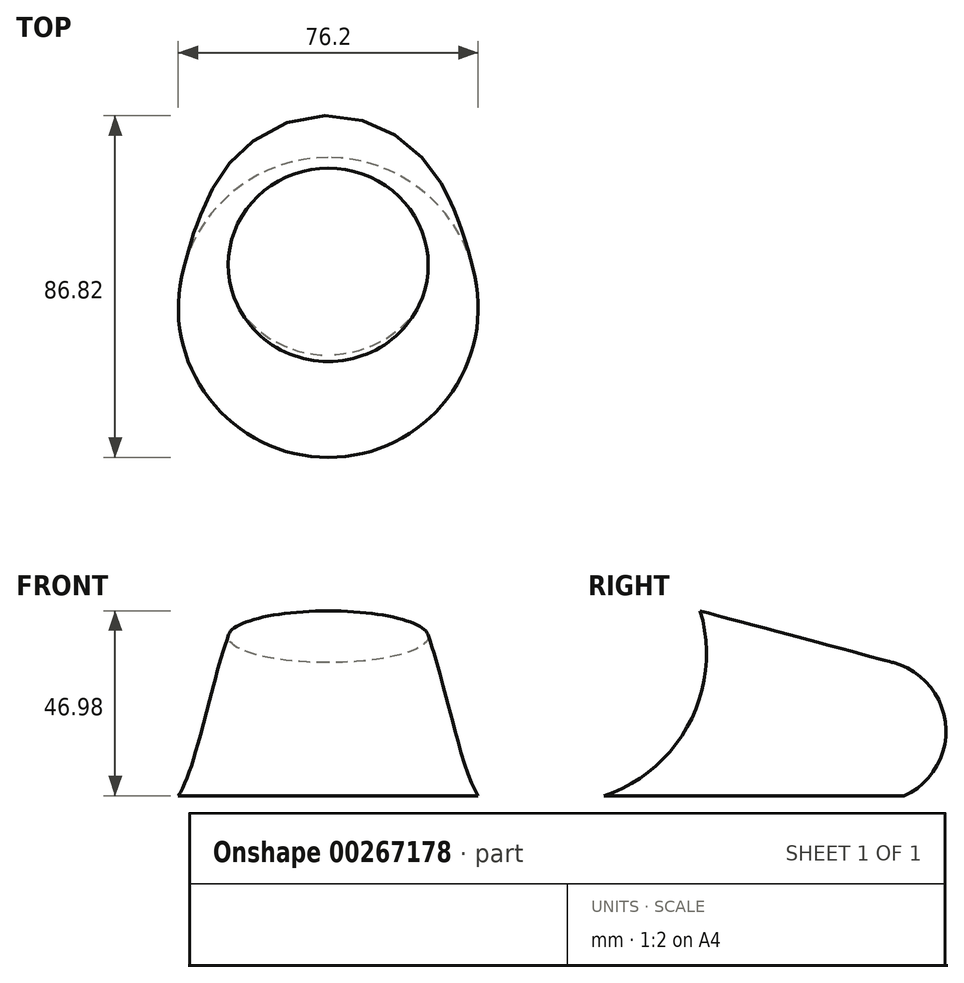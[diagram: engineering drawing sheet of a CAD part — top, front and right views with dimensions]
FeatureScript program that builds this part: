
annotation { "Feature Type Name" : "Feature", "Feature Type Description" : "" }
export const myFeature = defineFeature(function(context is Context, id is Id, definition is map)
    precondition{}
    {
        {
            var Q0;
            Q0=qCreatedBy(makeId("Top.planeOp"),FACE);
            var sketch = newSketch(context, id + "F0", { "sketchPlane" : qUnion([Q0])});
            skCircle(sketch, "E0", {"center": v(0, 0) * mm, "radius": 38.1 * mm});
            skLineSegment(sketch, "E1", {"start": v(-63.5, 63.5) * mm, "end": v(63.5, 63.5) * mm, "construction": true});
            skSolve(sketch);
        }
        {
            var Q0;
            Q0=sQuery(id+"F0.wireOp",EDGE,"E1");
            cPlane(context, id + "F1", {"entities" : qUnion([Q0]), "cplaneType" : CPlaneType.LINE_ANGLE, "offset" : 25.4 * mm, "angle" : 75 * degree, "width" : 152.4 * mm, "height" : 152.4 * mm});
        }
        {
            var Q0;
            Q0=qCreatedBy(id+"F1.planeOp",FACE);
            cPlane(context, id + "F2", {"entities" : qUnion([Q0]), "cplaneType" : CPlaneType.OFFSET, "offset" : 25.4 * mm, "width" : 152.4 * mm, "height" : 152.4 * mm});
        }
        {
            var Q0;
            Q0=qCreatedBy(id+"F2.planeOp",FACE);
            var sketch = newSketch(context, id + "F3", { "sketchPlane" : qUnion([Q0])});
            skCircle(sketch, "E2", {"center": v(0, 0) * mm, "radius": 25.4 * mm});
            skSolve(sketch);
        }
        {
            var Q0;
            Q0=qCreatedBy(makeId("Right.planeOp"),FACE);
            var sketch = newSketch(context, id + "F4", { "sketchPlane" : qUnion([Q0])});
            skLineSegment(sketch, "E3.0", {"start": v(-13.7, 46.98) * mm, "end": v(35.36, 33.84) * mm});
            skLineSegment(sketch, "E3.1", {"start": v(-38.1, 0) * mm, "end": v(38.1, 0) * mm});
            skArc(sketch, "E4", {"start": v(-38.1, 0) * mm, "mid": v(-16.41, 18.56) * mm, "end": v(-13.7, 46.98) * mm});
            skArc(sketch, "E5", {"start": v(35.36, 33.84) * mm, "mid": v(48.66, 17.88) * mm, "end": v(38.1, 0) * mm});
            skSolve(sketch);
        }
        {
            var Q0;
            Q0=makeQuery(id+"F0.imprint","IMPRINT",FACE,{"disambiguationData":[TD([[makeQuery(id+"F0.imprint","IMPRINT",EDGE,{"derivedFrom":sQuery(id+"F0.wireOp",EDGE,"E0")}),1.0]])]});
            var Q1;
            Q1=makeQuery(id+"F3.imprint","IMPRINT",FACE,{"disambiguationData":[TD([[makeQuery(id+"F3.imprint","IMPRINT",EDGE,{"derivedFrom":sQuery(id+"F3.wireOp",EDGE,"E2")}),1.0]])]});
            var Q2;
            Q2=sQuery(id+"F4.wireOp",EDGE,"E4");
            var Q3;
            Q3=sQuery(id+"F4.wireOp",EDGE,"E5");
            loft(context, id + "F5", {"addGuides" : true, "sheetProfilesArray" : [{ "sheetProfileEntities" : qUnion([Q0]) }, { "sheetProfileEntities" : qUnion([Q1]) }], "guidesArray" : [{ "guideEntities" : qUnion([Q2]), "guideDerivativeType" : LoftGuideDerivativeType.DEFAULT, "guideDerivativeMagnitude" : 1 }, { "guideEntities" : qUnion([Q3]), "guideDerivativeType" : LoftGuideDerivativeType.DEFAULT, "guideDerivativeMagnitude" : 1 }]});
        }
    });
